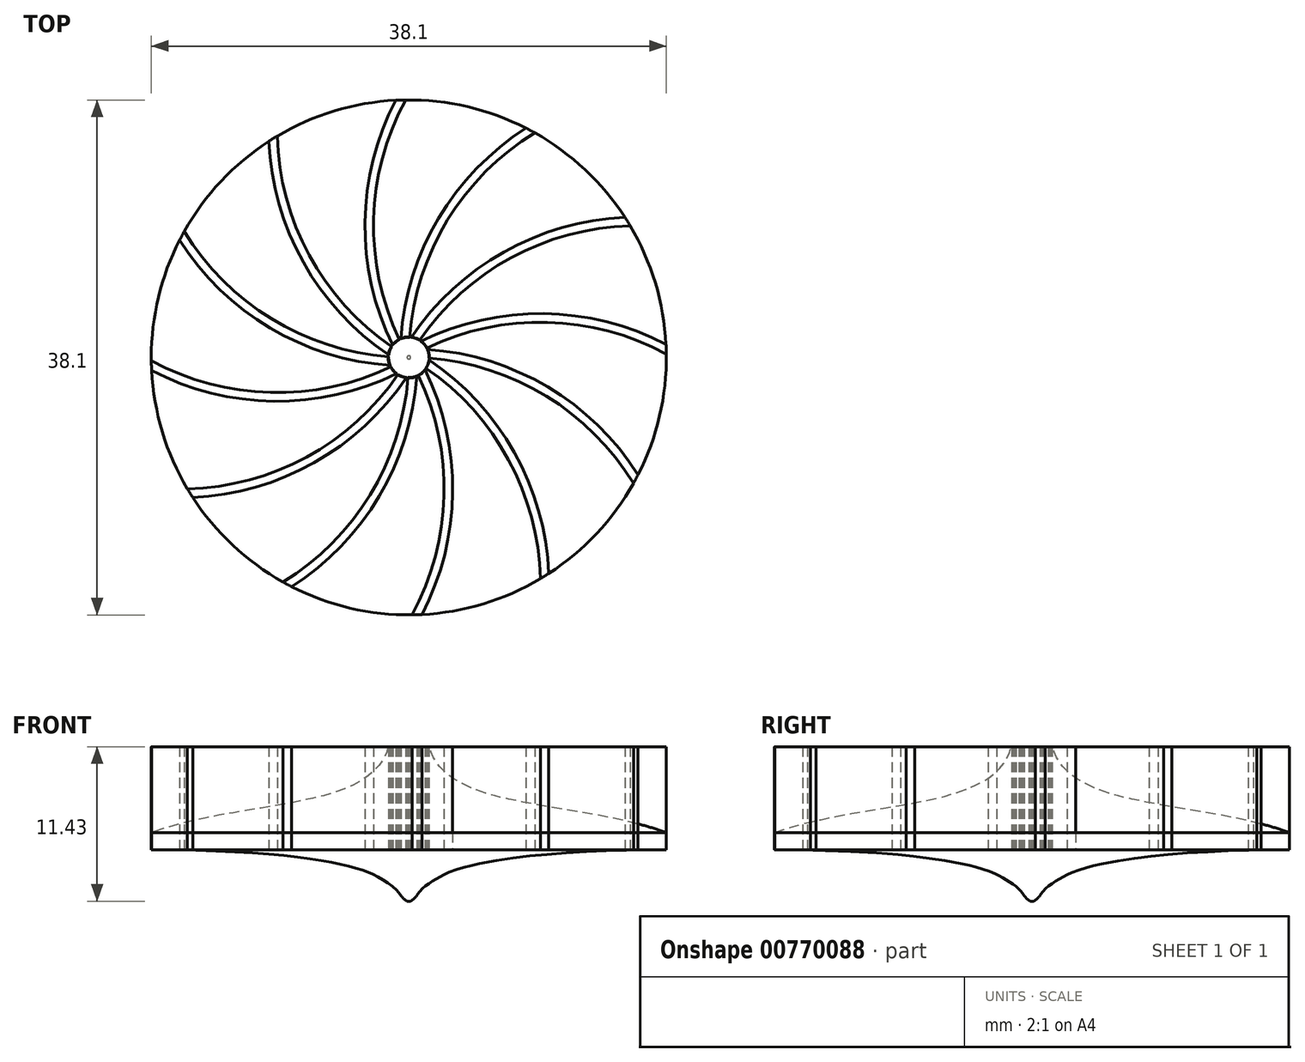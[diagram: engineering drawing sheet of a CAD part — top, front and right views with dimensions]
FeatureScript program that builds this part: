
annotation { "Feature Type Name" : "Feature", "Feature Type Description" : "" }
export const myFeature = defineFeature(function(context is Context, id is Id, definition is map)
    precondition{}
    {
        {
            var Q0;
            Q0=qCreatedBy(makeId("Top.planeOp"),FACE);
            var sketch = newSketch(context, id + "F0", { "sketchPlane" : qUnion([Q0])});
            skCircle(sketch, "E0", {"center": v(0, 0) * mm, "radius": 19.05 * mm});
            skPoint(sketch, "E1", {"position": v(-0.24, 19.05) * mm});
            skPoint(sketch, "E2.1.0", {"position": v(-9.73, 16.38) * mm});
            skPoint(sketch, "E2.2.0", {"position": v(-16.62, 9.32) * mm});
            skPoint(sketch, "E3.0.3.0", {"position": v(-19.05, -0.24) * mm});
            skPoint(sketch, "E3.0.4.0", {"position": v(-16.38, -9.73) * mm});
            skPoint(sketch, "E3.0.5.0", {"position": v(-9.32, -16.62) * mm});
            skPoint(sketch, "E3.0.6.0", {"position": v(0.24, -19.05) * mm});
            skPoint(sketch, "E3.0.7.0", {"position": v(9.73, -16.38) * mm});
            skPoint(sketch, "E3.0.8.0", {"position": v(16.62, -9.32) * mm});
            skPoint(sketch, "E3.0.9.0", {"position": v(19.05, 0.24) * mm});
            skPoint(sketch, "E3.0.10.0", {"position": v(16.38, 9.73) * mm});
            skPoint(sketch, "E3.0.11.0", {"position": v(9.32, 16.62) * mm});
            skArc(sketch, "E4", {"start": v(9.32, 16.62) * mm, "mid": v(2.49, 9.53) * mm, "end": v(0, 0) * mm});
            skArc(sketch, "E5.0", {"start": v(8.67, 16.96) * mm, "mid": v(1.84, 9.67) * mm, "end": v(-0.63, 0) * mm});
            skArc(sketch, "E6.1.0", {"start": v(-0.24, 19.05) * mm, "mid": v(-2.6, 9.5) * mm, "end": v(0, 0) * mm});
            skArc(sketch, "E6.1.1", {"start": v(-0.97, 19.03) * mm, "mid": v(-3.24, 9.3) * mm, "end": v(-0.55, -0.32) * mm});
            skArc(sketch, "E6.2.0", {"start": v(-9.73, 16.38) * mm, "mid": v(-7, 6.92) * mm, "end": v(0, 0) * mm});
            skArc(sketch, "E6.2.1", {"start": v(-10.35, 16) * mm, "mid": v(-7.46, 6.43) * mm, "end": v(-0.32, -0.55) * mm});
            skArc(sketch, "E6.3.0", {"start": v(-16.62, 9.32) * mm, "mid": v(-9.53, 2.49) * mm, "end": v(0, 0) * mm});
            skArc(sketch, "E6.3.1", {"start": v(-16.96, 8.67) * mm, "mid": v(-9.67, 1.84) * mm, "end": v(0, -0.63) * mm});
            skArc(sketch, "E6.4.0", {"start": v(-19.05, -0.24) * mm, "mid": v(-9.5, -2.6) * mm, "end": v(0, 0) * mm});
            skArc(sketch, "E6.4.1", {"start": v(-19.03, -0.97) * mm, "mid": v(-9.3, -3.24) * mm, "end": v(0.32, -0.55) * mm});
            skArc(sketch, "E6.5.0", {"start": v(-16.38, -9.73) * mm, "mid": v(-6.92, -7) * mm, "end": v(0, 0) * mm});
            skArc(sketch, "E6.5.1", {"start": v(-16, -10.35) * mm, "mid": v(-6.43, -7.46) * mm, "end": v(0.55, -0.32) * mm});
            skArc(sketch, "E6.6.0", {"start": v(-9.32, -16.62) * mm, "mid": v(-2.49, -9.53) * mm, "end": v(0, 0) * mm});
            skArc(sketch, "E6.6.1", {"start": v(-8.67, -16.96) * mm, "mid": v(-1.84, -9.67) * mm, "end": v(0.63, 0) * mm});
            skArc(sketch, "E6.7.0", {"start": v(0.24, -19.05) * mm, "mid": v(2.6, -9.5) * mm, "end": v(0, 0) * mm});
            skArc(sketch, "E6.7.1", {"start": v(0.97, -19.03) * mm, "mid": v(3.24, -9.3) * mm, "end": v(0.55, 0.32) * mm});
            skArc(sketch, "E6.8.0", {"start": v(9.73, -16.38) * mm, "mid": v(7, -6.92) * mm, "end": v(0, 0) * mm});
            skArc(sketch, "E6.8.1", {"start": v(10.35, -16) * mm, "mid": v(7.46, -6.43) * mm, "end": v(0.32, 0.55) * mm});
            skArc(sketch, "E6.9.0", {"start": v(16.62, -9.32) * mm, "mid": v(9.53, -2.49) * mm, "end": v(0, 0) * mm});
            skArc(sketch, "E6.9.1", {"start": v(16.96, -8.67) * mm, "mid": v(9.67, -1.84) * mm, "end": v(0, 0.63) * mm});
            skArc(sketch, "E6.10.0", {"start": v(19.05, 0.24) * mm, "mid": v(9.5, 2.6) * mm, "end": v(0, 0) * mm});
            skArc(sketch, "E6.10.1", {"start": v(19.03, 0.97) * mm, "mid": v(9.3, 3.24) * mm, "end": v(-0.32, 0.55) * mm});
            skArc(sketch, "E6.11.0", {"start": v(16.38, 9.73) * mm, "mid": v(6.92, 7) * mm, "end": v(0, 0) * mm});
            skArc(sketch, "E6.11.1", {"start": v(16, 10.35) * mm, "mid": v(6.43, 7.46) * mm, "end": v(-0.55, 0.32) * mm});
            skCircle(sketch, "E7", {"center": v(0, 0) * mm, "radius": 1.5 * mm});
            skSolve(sketch);
        }
        {
            var Q0;
            Q0=qCreatedBy(makeId("Top.planeOp"),FACE);
            var sketch = newSketch(context, id + "F1", { "sketchPlane" : qUnion([Q0])});
            skCircle(sketch, "E8", {"center": v(0, 0) * mm, "radius": 19.05 * mm});
            skSolve(sketch);
        }
        {
            var Q0;
            Q0=qSketchRegion(id+"F1",true);
            extrude(context, id + "F2", {"entities" : qUnion([Q0]), "depth" : 6.35 * mm, "offsetDistance" : 25.4 * mm, "hasSecondDirection" : true, "secondDirectionOppositeDirection" : true, "secondDirectionDepth" : 1.27 * mm});
        }
        {
            var Q0;
            Q0=qCreatedBy(makeId("Front.planeOp"),FACE);
            var sketch = newSketch(context, id + "F3", { "sketchPlane" : qUnion([Q0])});
            skLineSegment(sketch, "E9.bottom", {"start": v(19.05, 6.35) * mm, "end": v(-19.05, 6.35) * mm});
            skLineSegment(sketch, "E9.left", {"start": v(19.05, 6.35) * mm, "end": v(19.05, -5.08) * mm});
            skLineSegment(sketch, "E9.right", {"start": v(-19.05, 6.35) * mm, "end": v(-19.05, -5.08) * mm});
            skPoint(sketch, "E9.middle", {"position": v(0, 0) * mm});
            skLineSegment(sketch, "E10", {"start": v(-19.05, -5.08) * mm, "end": v(19.05, -5.08) * mm});
            skLineSegment(sketch, "E11", {"start": v(-19.05, 0) * mm, "end": v(19.05, 0) * mm, "construction": true});
            skLineSegment(sketch, "E12", {"start": v(0, -5.08) * mm, "end": v(0, 6.35) * mm, "construction": true});
            skPoint(sketch, "E13", {"position": v(1.52, 6.35) * mm});
            skPoint(sketch, "E14", {"position": v(19.05, 1.27) * mm});
            skFitSpline(sketch, "E15", {"points": [v(1.52, 6.35) * mm, v(5.08, 3.11) * mm, v(19.05, 0) * mm, v(28.85, -6.98) * mm], "startDerivative": vector(3.87, -17.8) * mm, "endDerivative": vector(21.57, -22.67) * mm});
            skLineSegment(sketch, "E16", {"start": v(1.52, 6.35) * mm, "end": v(19.05, 6.35) * mm});
            skFitSpline(sketch, "E17", {"points": [v(19.05, -1.28) * mm, v(4.25, -2.54) * mm, v(2.03, -3.42) * mm, v(0.5, -4.83) * mm], "startDerivative": vector(-41.63, 0) * mm, "endDerivative": vector(-3.76, -8.36) * mm});
            skArc(sketch, "E18", {"start": v(0.13, -5.08) * mm, "mid": v(0.4, -4.87) * mm, "end": v(0.64, -4.6) * mm});
            skLineSegment(sketch, "E19", {"start": v(0, -5.08) * mm, "end": v(0, -1.28) * mm});
            skLineSegment(sketch, "E20", {"start": v(0, -1.28) * mm, "end": v(19.05, -1.28) * mm});
            skSolve(sketch);
        }
        {
            var Q0;
            {var subQ0=sQuery(id+"F3.wireOp",EDGE,"E15");Q0=makeQuery(id+"F3.imprint","IMPRINT",FACE,{"disambiguationData":[TD([[makeQuery(id+"F3.imprint","IMPRINT",EDGE,{"derivedFrom":subQ0}),1.0]])]});}
            var Q1;
            Q1=sQuery(id+"F3.wireOp",EDGE,"E12");
            revolve(context, id + "F4", {"operationType" : NewBodyOperationType.REMOVE, "surfaceOperationType" : NewSurfaceOperationType.NEW, "entities" : qUnion([Q0]), "axis" : qUnion([Q1]), "revolveType" : RevolveType.FULL});
        }
        {
            var Q0;
            {var subQ0=sQuery(id+"F0.wireOp",EDGE,"E6.4.0");var subQ1=sQuery(id+"F0.wireOp",EDGE,"E0");var subQ2=makeQuery(id+"F0.imprint","INTERSECT",VERTEX,{"derivedFrom":[subQ1,subQ0]});Q0=makeQuery(id+"F0.imprint","IMPRINT",FACE,{"disambiguationData":[TD([[makeQuery(id+"F0.imprint","IMPRINT",EDGE,{"disambiguationData":[TD([[subQ2,-1.0]])],"derivedFrom":subQ1}),1.0]])]});}
            var Q1;
            {var subQ0=sQuery(id+"F0.wireOp",EDGE,"E6.9.0");var subQ1=sQuery(id+"F0.wireOp",EDGE,"E0");var subQ2=makeQuery(id+"F0.imprint","INTERSECT",VERTEX,{"derivedFrom":[subQ1,subQ0]});Q1=makeQuery(id+"F0.imprint","IMPRINT",FACE,{"disambiguationData":[TD([[makeQuery(id+"F0.imprint","IMPRINT",EDGE,{"disambiguationData":[TD([[subQ2,-1.0]])],"derivedFrom":subQ1}),1.0]])]});}
            var Q2;
            {var subQ0=sQuery(id+"F0.wireOp",EDGE,"E6.6.0");var subQ1=sQuery(id+"F0.wireOp",EDGE,"E0");var subQ2=makeQuery(id+"F0.imprint","INTERSECT",VERTEX,{"derivedFrom":[subQ1,subQ0]});Q2=makeQuery(id+"F0.imprint","IMPRINT",FACE,{"disambiguationData":[TD([[makeQuery(id+"F0.imprint","IMPRINT",EDGE,{"disambiguationData":[TD([[subQ2,-1.0]])],"derivedFrom":subQ1}),1.0]])]});}
            var Q3;
            {var subQ0=sQuery(id+"F0.wireOp",EDGE,"E6.10.0");var subQ1=sQuery(id+"F0.wireOp",EDGE,"E0");var subQ2=makeQuery(id+"F0.imprint","INTERSECT",VERTEX,{"derivedFrom":[subQ1,subQ0]});Q3=makeQuery(id+"F0.imprint","IMPRINT",FACE,{"disambiguationData":[TD([[makeQuery(id+"F0.imprint","IMPRINT",EDGE,{"disambiguationData":[TD([[subQ2,-1.0]])],"derivedFrom":subQ1}),1.0]])]});}
            var Q4;
            {var subQ0=sQuery(id+"F0.wireOp",EDGE,"E6.3.0");var subQ1=sQuery(id+"F0.wireOp",EDGE,"E0");var subQ2=makeQuery(id+"F0.imprint","INTERSECT",VERTEX,{"derivedFrom":[subQ1,subQ0]});Q4=makeQuery(id+"F0.imprint","IMPRINT",FACE,{"disambiguationData":[TD([[makeQuery(id+"F0.imprint","IMPRINT",EDGE,{"disambiguationData":[TD([[subQ2,-1.0]])],"derivedFrom":subQ1}),1.0]])]});}
            var Q5;
            {var subQ0=sQuery(id+"F0.wireOp",EDGE,"E6.8.0");var subQ1=sQuery(id+"F0.wireOp",EDGE,"E0");var subQ2=makeQuery(id+"F0.imprint","INTERSECT",VERTEX,{"derivedFrom":[subQ1,subQ0]});Q5=makeQuery(id+"F0.imprint","IMPRINT",FACE,{"disambiguationData":[TD([[makeQuery(id+"F0.imprint","IMPRINT",EDGE,{"disambiguationData":[TD([[subQ2,-1.0]])],"derivedFrom":subQ1}),1.0]])]});}
            var Q6;
            {var subQ0=sQuery(id+"F0.wireOp",EDGE,"E6.7.0");var subQ1=sQuery(id+"F0.wireOp",EDGE,"E0");var subQ2=makeQuery(id+"F0.imprint","INTERSECT",VERTEX,{"derivedFrom":[subQ1,subQ0]});Q6=makeQuery(id+"F0.imprint","IMPRINT",FACE,{"disambiguationData":[TD([[makeQuery(id+"F0.imprint","IMPRINT",EDGE,{"disambiguationData":[TD([[subQ2,-1.0]])],"derivedFrom":subQ1}),1.0]])]});}
            var Q7;
            {var subQ0=sQuery(id+"F0.wireOp",EDGE,"E6.11.0");var subQ1=sQuery(id+"F0.wireOp",EDGE,"E0");var subQ2=makeQuery(id+"F0.imprint","INTERSECT",VERTEX,{"derivedFrom":[subQ1,subQ0]});Q7=makeQuery(id+"F0.imprint","IMPRINT",FACE,{"disambiguationData":[TD([[makeQuery(id+"F0.imprint","IMPRINT",EDGE,{"disambiguationData":[TD([[subQ2,-1.0]])],"derivedFrom":subQ1}),1.0]])]});}
            var Q8;
            {var subQ0=sQuery(id+"F0.wireOp",EDGE,"E6.1.0");var subQ1=sQuery(id+"F0.wireOp",EDGE,"E0");var subQ2=makeQuery(id+"F0.imprint","INTERSECT",VERTEX,{"derivedFrom":[subQ1,subQ0]});Q8=makeQuery(id+"F0.imprint","IMPRINT",FACE,{"disambiguationData":[TD([[makeQuery(id+"F0.imprint","IMPRINT",EDGE,{"disambiguationData":[TD([[subQ2,-1.0]])],"derivedFrom":subQ1}),1.0]])]});}
            var Q9;
            {var subQ0=sQuery(id+"F0.wireOp",EDGE,"E6.5.0");var subQ1=sQuery(id+"F0.wireOp",EDGE,"E0");var subQ2=makeQuery(id+"F0.imprint","INTERSECT",VERTEX,{"derivedFrom":[subQ1,subQ0]});Q9=makeQuery(id+"F0.imprint","IMPRINT",FACE,{"disambiguationData":[TD([[makeQuery(id+"F0.imprint","IMPRINT",EDGE,{"disambiguationData":[TD([[subQ2,-1.0]])],"derivedFrom":subQ1}),1.0]])]});}
            var Q10;
            {var subQ0=sQuery(id+"F0.wireOp",EDGE,"E4");var subQ1=sQuery(id+"F0.wireOp",EDGE,"E0");var subQ2=makeQuery(id+"F0.imprint","INTERSECT",VERTEX,{"derivedFrom":[subQ1,subQ0]});Q10=makeQuery(id+"F0.imprint","IMPRINT",FACE,{"disambiguationData":[TD([[makeQuery(id+"F0.imprint","IMPRINT",EDGE,{"disambiguationData":[TD([[subQ2,-1.0]])],"derivedFrom":subQ1}),1.0]])]});}
            var Q11;
            {var subQ0=sQuery(id+"F0.wireOp",EDGE,"E6.2.0");var subQ1=sQuery(id+"F0.wireOp",EDGE,"E0");var subQ2=makeQuery(id+"F0.imprint","INTERSECT",VERTEX,{"derivedFrom":[subQ1,subQ0]});Q11=makeQuery(id+"F0.imprint","IMPRINT",FACE,{"disambiguationData":[TD([[makeQuery(id+"F0.imprint","IMPRINT",EDGE,{"disambiguationData":[TD([[subQ2,-1.0]])],"derivedFrom":subQ1}),1.0]])]});}
            extrude(context, id + "F5", {"entities" : qUnion([Q0, Q1, Q2, Q3, Q4, Q5, Q6, Q7, Q8, Q9, Q10, Q11]), "depth" : 6.35 * mm, "offsetDistance" : 25.4 * mm, "hasSecondDirection" : true, "secondDirectionOppositeDirection" : true, "secondDirectionDepth" : 1.27 * mm});
        }
        {
            var Q0;
            {var subQ1=sQuery(id+"F3.wireOp",EDGE,"E9.right");Q0=makeQuery(id+"F3.imprint","IMPRINT",FACE,{"disambiguationData":[TD([[makeQuery(id+"F3.imprint","IMPRINT",EDGE,{"derivedFrom":subQ1}),1.0]])]});}
            var sketch = newSketch(context, id + "F6", { "sketchPlane" : qUnion([Q0])});
            skLineSegment(sketch, "E21.bottom", {"start": v(-19.05, -4.25) * mm, "end": v(19.05, -4.25) * mm});
            skLineSegment(sketch, "E21.top", {"start": v(-19.05, -1.27) * mm, "end": v(19.05, -1.27) * mm});
            skLineSegment(sketch, "E21.left", {"start": v(-19.05, -4.25) * mm, "end": v(-19.05, -1.27) * mm});
            skLineSegment(sketch, "E21.right", {"start": v(19.05, -4.25) * mm, "end": v(19.05, -1.27) * mm});
            skPoint(sketch, "E22", {"position": v(0, -4.25) * mm});
            skSolve(sketch);
        }
        {
            var Q0;
            {var subQ7=sQuery(id+"F6.wireOp",EDGE,"E21.top");Q0=makeQuery(id+"F6.imprint","IMPRINT",FACE,{"disambiguationData":[TD([[makeQuery(id+"F6.imprint","IMPRINT",EDGE,{"derivedFrom":subQ7}),-1.0]])]});}
            var Q1;
            {var subQ0=sQuery(id+"F6.wireOp",EDGE,"E21.right");var subQ1=sQuery(id+"F6.wireOp",EDGE,"E21.bottom");var subQ2=makeQuery(id+"F6.imprint","INTERSECT",VERTEX,{"derivedFrom":[subQ1,subQ0]});Q1=makeQuery(id+"F6.imprint","IMPRINT",FACE,{"disambiguationData":[TD([[makeQuery(id+"F6.imprint","IMPRINT",EDGE,{"disambiguationData":[TD([[subQ2,1.0]])],"derivedFrom":subQ1}),1.0]])]});}
            extrude(context, id + "F7", {"entities" : qUnion([Q0, Q1]), "operationType" : NewBodyOperationType.REMOVE, "endBound" : BoundingType.SYMMETRIC, "oppositeDirection" : true, "depth" : 127 * mm, "offsetDistance" : 25.4 * mm, "hasSecondDirection" : true, "secondDirectionBound" : SecondDirectionBoundingType.THROUGH_ALL, "secondDirectionOppositeDirection" : false, "secondDirectionDepth" : 25.4 * mm});
        }
        {
            var Q0;
            Q0=makeQuery(id+"F3.imprint","IMPRINT",FACE,{"disambiguationData":[TD([[makeQuery(id+"F3.imprint","IMPRINT",EDGE,{"derivedFrom":sQuery(id+"F3.wireOp",EDGE,"E17")}),-1.0]])]});
            var Q1;
            Q1=sQuery(id+"F3.wireOp",EDGE,"E12");
            revolve(context, id + "F8", {"surfaceOperationType" : NewSurfaceOperationType.NEW, "entities" : qUnion([Q0]), "axis" : qUnion([Q1]), "revolveType" : RevolveType.FULL});
        }
    });
